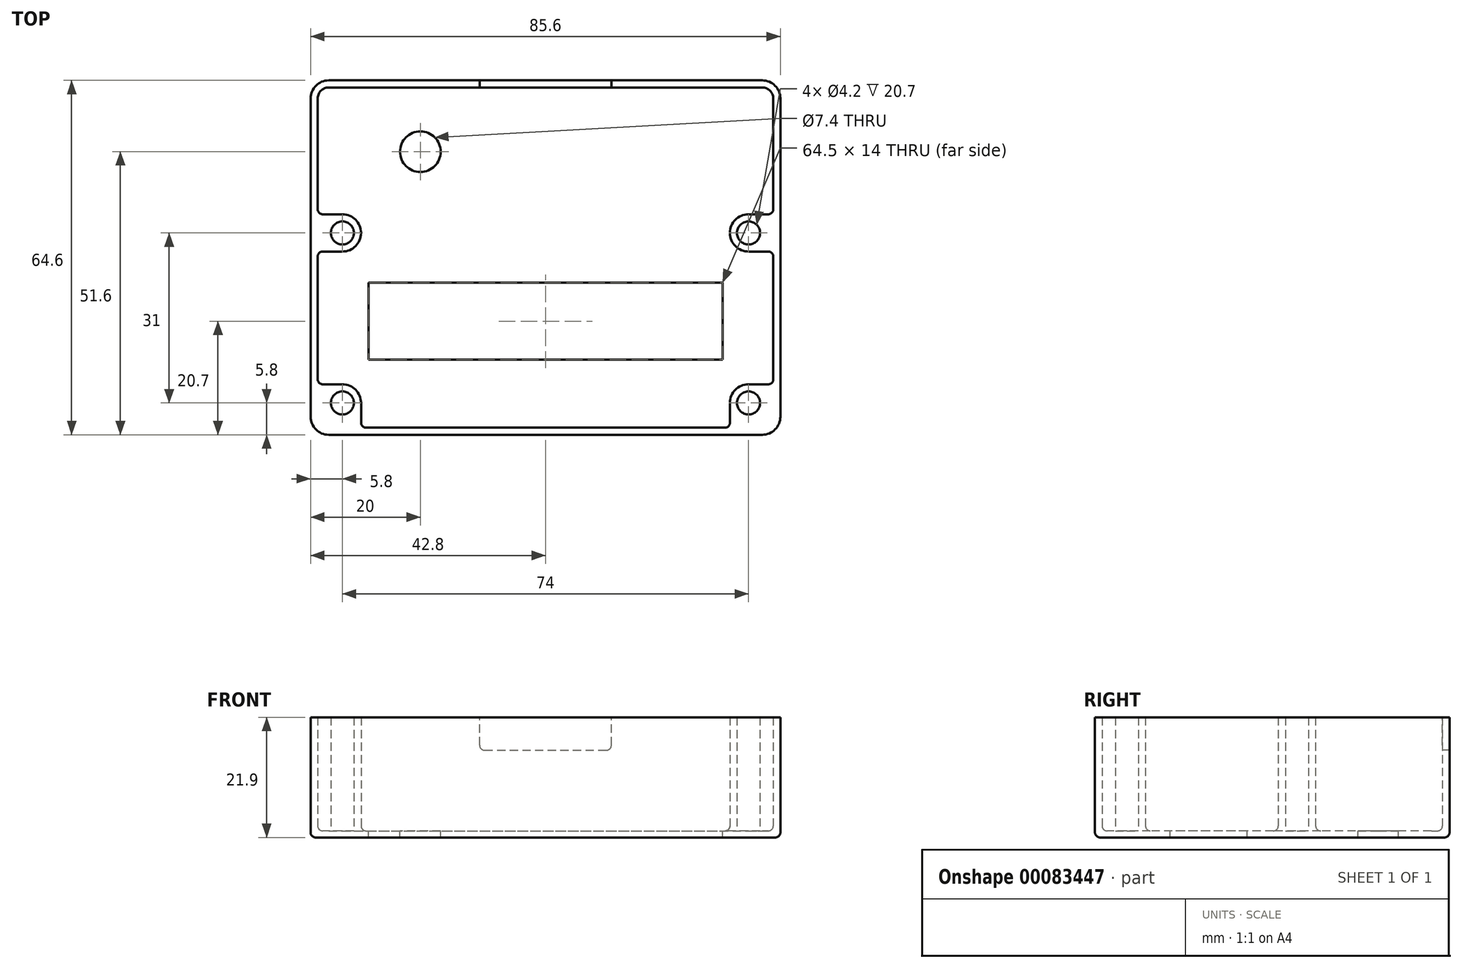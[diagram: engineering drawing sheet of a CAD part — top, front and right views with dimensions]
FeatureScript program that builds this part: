
annotation { "Feature Type Name" : "Feature", "Feature Type Description" : "" }
export const myFeature = defineFeature(function(context is Context, id is Id, definition is map)
    precondition{}
    {
        {
            var Q0;
            Q0=qCreatedBy(makeId("Top.planeOp"),FACE);
            var sketch = newSketch(context, id + "F0", { "sketchPlane" : qUnion([Q0])});
            skLineSegment(sketch, "E0.bottom", {"start": v(-37, 15.5) * mm, "end": v(37, 15.5) * mm, "construction": true});
            skLineSegment(sketch, "E0.top", {"start": v(-37, -15.5) * mm, "end": v(37, -15.5) * mm, "construction": true});
            skLineSegment(sketch, "E0.left", {"start": v(-37, 15.5) * mm, "end": v(-37, -15.5) * mm, "construction": true});
            skLineSegment(sketch, "E0.right", {"start": v(37, 15.5) * mm, "end": v(37, -15.5) * mm, "construction": true});
            skCircle(sketch, "E1", {"center": v(-37, 15.5) * mm, "radius": 2.1 * mm});
            skCircle(sketch, "E2", {"center": v(37, 15.5) * mm, "radius": 2.1 * mm});
            skCircle(sketch, "E3", {"center": v(37, -15.5) * mm, "radius": 2.1 * mm});
            skCircle(sketch, "E4", {"center": v(-37, -15.5) * mm, "radius": 2.1 * mm});
            skLineSegment(sketch, "E5.bottom", {"start": v(-39.5, 42) * mm, "end": v(39.5, 42) * mm});
            skLineSegment(sketch, "E5.top", {"start": v(-39.5, -20) * mm, "end": v(39.5, -20) * mm});
            skLineSegment(sketch, "E5.left", {"start": v(-41.5, 40) * mm, "end": v(-41.5, -18) * mm});
            skLineSegment(sketch, "E5.right", {"start": v(41.5, 40) * mm, "end": v(41.5, -18) * mm});
            skPoint(sketch, "E6.visualSharp", {"position": v(-41.5, 42) * mm});
            skArc(sketch, "E6.filletArc", {"start": v(-39.5, 42) * mm, "mid": v(-40.91, 41.41) * mm, "end": v(-41.5, 40) * mm});
            skPoint(sketch, "E7.visualSharp", {"position": v(41.5, 42) * mm});
            skArc(sketch, "E7.filletArc", {"start": v(41.5, 40) * mm, "mid": v(40.91, 41.41) * mm, "end": v(39.5, 42) * mm});
            skPoint(sketch, "E8.visualSharp", {"position": v(41.5, -20) * mm});
            skArc(sketch, "E8.filletArc", {"start": v(39.5, -20) * mm, "mid": v(40.91, -19.41) * mm, "end": v(41.5, -18) * mm});
            skPoint(sketch, "E9.visualSharp", {"position": v(-41.5, -20) * mm});
            skArc(sketch, "E9.filletArc", {"start": v(-41.5, -18) * mm, "mid": v(-40.91, -19.41) * mm, "end": v(-39.5, -20) * mm});
            skArc(sketch, "E10.0", {"start": v(-39.5, 43.3) * mm, "mid": v(-41.83, 42.33) * mm, "end": v(-42.8, 40) * mm});
            skLineSegment(sketch, "E10.1", {"start": v(-42.8, 40) * mm, "end": v(-42.8, -18) * mm});
            skLineSegment(sketch, "E10.2", {"start": v(-39.5, 43.3) * mm, "end": v(39.5, 43.3) * mm});
            skArc(sketch, "E10.3", {"start": v(-42.8, -18) * mm, "mid": v(-41.83, -20.33) * mm, "end": v(-39.5, -21.3) * mm});
            skArc(sketch, "E10.4", {"start": v(42.8, 40) * mm, "mid": v(41.83, 42.33) * mm, "end": v(39.5, 43.3) * mm});
            skLineSegment(sketch, "E10.5", {"start": v(42.8, 40) * mm, "end": v(42.8, -18) * mm});
            skArc(sketch, "E10.6", {"start": v(39.5, -21.3) * mm, "mid": v(41.83, -20.33) * mm, "end": v(42.8, -18) * mm});
            skLineSegment(sketch, "E10.7", {"start": v(-39.5, -21.3) * mm, "end": v(39.5, -21.3) * mm});
            skCircle(sketch, "E11.0", {"center": v(-37, 15.5) * mm, "radius": 3.4 * mm});
            skCircle(sketch, "E12.0", {"center": v(37, 15.5) * mm, "radius": 3.4 * mm});
            skCircle(sketch, "E13.0", {"center": v(-37, -15.5) * mm, "radius": 3.4 * mm});
            skCircle(sketch, "E14.0", {"center": v(37, -15.5) * mm, "radius": 3.4 * mm});
            skLineSegment(sketch, "E15", {"start": v(-37, 12.1) * mm, "end": v(-41.5, 12.1) * mm});
            skLineSegment(sketch, "E16", {"start": v(-37, -12.1) * mm, "end": v(-41.5, -12.1) * mm});
            skLineSegment(sketch, "E17", {"start": v(-33.6, -15.5) * mm, "end": v(-33.6, -20) * mm});
            skLineSegment(sketch, "E18", {"start": v(-37, 18.9) * mm, "end": v(-41.5, 18.9) * mm});
            skLineSegment(sketch, "E19.MirrorCS", {"start": v(37, 18.9) * mm, "end": v(41.5, 18.9) * mm});
            skLineSegment(sketch, "E20.MirrorCS", {"start": v(37, 12.1) * mm, "end": v(41.5, 12.1) * mm});
            skLineSegment(sketch, "E21.MirrorCS", {"start": v(37, -12.1) * mm, "end": v(41.5, -12.1) * mm});
            skLineSegment(sketch, "E22.MirrorCS", {"start": v(33.6, -15.5) * mm, "end": v(33.6, -20) * mm});
            skSolve(sketch);
        }
        {
            var Q0;
            Q0=makeQuery(id+"F0.imprint","IMPRINT",FACE,{"disambiguationData":[TD([[makeQuery(id+"F0.imprint","IMPRINT",EDGE,{"derivedFrom":sQuery(id+"F0.wireOp",EDGE,"E2")}),-1.0]])]});
            var Q1;
            {var subQ0=sQuery(id+"F0.wireOp",EDGE,"E19.MirrorCS");Q1=makeQuery(id+"F0.imprint","IMPRINT",FACE,{"disambiguationData":[TD([[makeQuery(id+"F0.imprint","IMPRINT",EDGE,{"derivedFrom":subQ0}),-1.0]])]});}
            var Q2;
            Q2=makeQuery(id+"F0.imprint","IMPRINT",FACE,{"disambiguationData":[TD([[makeQuery(id+"F0.imprint","IMPRINT",EDGE,{"derivedFrom":sQuery(id+"F0.wireOp",EDGE,"E5.bottom")}),-1.0]])]});
            var Q3;
            Q3=makeQuery(id+"F0.imprint","IMPRINT",FACE,{"disambiguationData":[TD([[makeQuery(id+"F0.imprint","IMPRINT",EDGE,{"derivedFrom":sQuery(id+"F0.wireOp",EDGE,"E5.bottom")}),1.0]])]});
            var Q4;
            Q4=makeQuery(id+"F0.imprint","IMPRINT",FACE,{"disambiguationData":[TD([[makeQuery(id+"F0.imprint","IMPRINT",EDGE,{"derivedFrom":sQuery(id+"F0.wireOp",EDGE,"E3")}),-1.0]])]});
            var Q5;
            Q5=makeQuery(id+"F0.imprint","IMPRINT",FACE,{"disambiguationData":[TD([[makeQuery(id+"F0.imprint","IMPRINT",EDGE,{"derivedFrom":sQuery(id+"F0.wireOp",EDGE,"E3")}),1.0]])]});
            var Q6;
            Q6=makeQuery(id+"F0.imprint","IMPRINT",FACE,{"disambiguationData":[TD([[makeQuery(id+"F0.imprint","IMPRINT",EDGE,{"derivedFrom":sQuery(id+"F0.wireOp",EDGE,"E2")}),1.0]])]});
            var Q7;
            {var subQ0=sQuery(id+"F0.wireOp",EDGE,"E8.filletArc");Q7=makeQuery(id+"F0.imprint","IMPRINT",FACE,{"disambiguationData":[TD([[makeQuery(id+"F0.imprint","IMPRINT",EDGE,{"derivedFrom":subQ0}),1.0]])]});}
            var Q8;
            Q8=makeQuery(id+"F0.imprint","IMPRINT",FACE,{"disambiguationData":[TD([[makeQuery(id+"F0.imprint","IMPRINT",EDGE,{"derivedFrom":sQuery(id+"F0.wireOp",EDGE,"E1")}),1.0]])]});
            var Q9;
            Q9=makeQuery(id+"F0.imprint","IMPRINT",FACE,{"disambiguationData":[TD([[makeQuery(id+"F0.imprint","IMPRINT",EDGE,{"derivedFrom":sQuery(id+"F0.wireOp",EDGE,"E1")}),-1.0]])]});
            var Q10;
            {var subQ0=sQuery(id+"F0.wireOp",EDGE,"E15");Q10=makeQuery(id+"F0.imprint","IMPRINT",FACE,{"disambiguationData":[TD([[makeQuery(id+"F0.imprint","IMPRINT",EDGE,{"derivedFrom":subQ0}),-1.0]])]});}
            var Q11;
            Q11=makeQuery(id+"F0.imprint","IMPRINT",FACE,{"disambiguationData":[TD([[makeQuery(id+"F0.imprint","IMPRINT",EDGE,{"derivedFrom":sQuery(id+"F0.wireOp",EDGE,"E4")}),1.0]])]});
            var Q12;
            Q12=makeQuery(id+"F0.imprint","IMPRINT",FACE,{"disambiguationData":[TD([[makeQuery(id+"F0.imprint","IMPRINT",EDGE,{"derivedFrom":sQuery(id+"F0.wireOp",EDGE,"E4")}),-1.0]])]});
            var Q13;
            {var subQ3=sQuery(id+"F0.wireOp",EDGE,"E9.filletArc");Q13=makeQuery(id+"F0.imprint","IMPRINT",FACE,{"disambiguationData":[TD([[makeQuery(id+"F0.imprint","IMPRINT",EDGE,{"derivedFrom":subQ3}),1.0]])]});}
            extrude(context, id + "F1", {"entities" : qUnion([Q0, Q1, Q2, Q3, Q4, Q5, Q6, Q7, Q8, Q9, Q10, Q11, Q12, Q13]), "oppositeDirection" : true, "depth" : 1.2 * mm});
        }
        {
            var Q0;
            Q0=makeQuery(id+"F0.imprint","IMPRINT",FACE,{"disambiguationData":[TD([[makeQuery(id+"F0.imprint","IMPRINT",EDGE,{"derivedFrom":sQuery(id+"F0.wireOp",EDGE,"E5.bottom")}),1.0]])]});
            var Q1;
            {var subQ0=sQuery(id+"F0.wireOp",EDGE,"E15");Q1=makeQuery(id+"F0.imprint","IMPRINT",FACE,{"disambiguationData":[TD([[makeQuery(id+"F0.imprint","IMPRINT",EDGE,{"derivedFrom":subQ0}),-1.0]])]});}
            var Q2;
            Q2=makeQuery(id+"F0.imprint","IMPRINT",FACE,{"disambiguationData":[TD([[makeQuery(id+"F0.imprint","IMPRINT",EDGE,{"derivedFrom":sQuery(id+"F0.wireOp",EDGE,"E1")}),-1.0]])]});
            var Q3;
            Q3=makeQuery(id+"F0.imprint","IMPRINT",FACE,{"disambiguationData":[TD([[makeQuery(id+"F0.imprint","IMPRINT",EDGE,{"derivedFrom":sQuery(id+"F0.wireOp",EDGE,"E2")}),-1.0]])]});
            var Q4;
            {var subQ0=sQuery(id+"F0.wireOp",EDGE,"E19.MirrorCS");Q4=makeQuery(id+"F0.imprint","IMPRINT",FACE,{"disambiguationData":[TD([[makeQuery(id+"F0.imprint","IMPRINT",EDGE,{"derivedFrom":subQ0}),-1.0]])]});}
            var Q5;
            {var subQ3=sQuery(id+"F0.wireOp",EDGE,"E9.filletArc");Q5=makeQuery(id+"F0.imprint","IMPRINT",FACE,{"disambiguationData":[TD([[makeQuery(id+"F0.imprint","IMPRINT",EDGE,{"derivedFrom":subQ3}),1.0]])]});}
            var Q6;
            Q6=makeQuery(id+"F0.imprint","IMPRINT",FACE,{"disambiguationData":[TD([[makeQuery(id+"F0.imprint","IMPRINT",EDGE,{"derivedFrom":sQuery(id+"F0.wireOp",EDGE,"E4")}),-1.0]])]});
            var Q7;
            {var subQ0=sQuery(id+"F0.wireOp",EDGE,"E8.filletArc");Q7=makeQuery(id+"F0.imprint","IMPRINT",FACE,{"disambiguationData":[TD([[makeQuery(id+"F0.imprint","IMPRINT",EDGE,{"derivedFrom":subQ0}),1.0]])]});}
            var Q8;
            Q8=makeQuery(id+"F0.imprint","IMPRINT",FACE,{"disambiguationData":[TD([[makeQuery(id+"F0.imprint","IMPRINT",EDGE,{"derivedFrom":sQuery(id+"F0.wireOp",EDGE,"E3")}),-1.0]])]});
            extrude(context, id + "F2", {"entities" : qUnion([Q0, Q1, Q2, Q3, Q4, Q5, Q6, Q7, Q8]), "operationType" : NewBodyOperationType.ADD, "depth" : 20.7 * mm});
        }
        {
            var Q0;
            Q0=makeQuery(id+"F2.opExtrude","CAP_FACE",FACE,{"disambiguationData":[OSD([sQuery(id+"F0.wireOp",EDGE,"E1"),sQuery(id+"F0.wireOp",EDGE,"E2"),sQuery(id+"F0.wireOp",EDGE,"E3"),sQuery(id+"F0.wireOp",EDGE,"E4"),sQuery(id+"F0.wireOp",EDGE,"E5.bottom"),sQuery(id+"F0.wireOp",EDGE,"E5.top"),sQuery(id+"F0.wireOp",EDGE,"E5.left"),sQuery(id+"F0.wireOp",EDGE,"E5.right"),sQuery(id+"F0.wireOp",EDGE,"E6.filletArc"),sQuery(id+"F0.wireOp",EDGE,"E7.filletArc"),sQuery(id+"F0.wireOp",EDGE,"E10.0"),sQuery(id+"F0.wireOp",EDGE,"E10.1"),sQuery(id+"F0.wireOp",EDGE,"E10.2"),sQuery(id+"F0.wireOp",EDGE,"E10.3"),sQuery(id+"F0.wireOp",EDGE,"E10.4"),sQuery(id+"F0.wireOp",EDGE,"E10.5"),sQuery(id+"F0.wireOp",EDGE,"E10.6"),sQuery(id+"F0.wireOp",EDGE,"E10.7"),sQuery(id+"F0.wireOp",EDGE,"E11.0"),sQuery(id+"F0.wireOp",EDGE,"E12.0"),sQuery(id+"F0.wireOp",EDGE,"E13.0"),sQuery(id+"F0.wireOp",EDGE,"E14.0"),sQuery(id+"F0.wireOp",EDGE,"E15"),sQuery(id+"F0.wireOp",EDGE,"E16"),sQuery(id+"F0.wireOp",EDGE,"E17"),sQuery(id+"F0.wireOp",EDGE,"E18"),sQuery(id+"F0.wireOp",EDGE,"E19.MirrorCS"),sQuery(id+"F0.wireOp",EDGE,"E20.MirrorCS"),sQuery(id+"F0.wireOp",EDGE,"E21.MirrorCS"),sQuery(id+"F0.wireOp",EDGE,"E22.MirrorCS")])],"isStart":false});
            var sketch = newSketch(context, id + "F3", { "sketchPlane" : qUnion([Q0])});
            skLineSegment(sketch, "E23", {"start": v(-12, 43.3) * mm, "end": v(-12, 42) * mm});
            skLineSegment(sketch, "E24.MirrorCS", {"start": v(12, 43.3) * mm, "end": v(12, 42) * mm});
            skLineSegment(sketch, "E25.0", {"start": v(-39.5, 43.3) * mm, "end": v(39.5, 43.3) * mm});
            skLineSegment(sketch, "E26.0", {"start": v(-39.5, 42) * mm, "end": v(39.5, 42) * mm});
            skSolve(sketch);
        }
        {
            var Q0;
            {var subQ0=sQuery(id+"F3.wireOp",EDGE,"E23");Q0=makeQuery(id+"F3.imprint","IMPRINT",FACE,{"disambiguationData":[TD([[makeQuery(id+"F3.imprint","IMPRINT",EDGE,{"derivedFrom":subQ0}),1.0]])]});}
            extrude(context, id + "F4", {"entities" : qUnion([Q0]), "operationType" : NewBodyOperationType.REMOVE, "oppositeDirection" : true, "depth" : 6 * mm});
        }
        {
            var Q0;
            Q0=makeQuery(id+"F2.opExtrude","SWEPT_EDGE",EDGE,{"disambiguationData":[OSD([sQuery(id+"F0.wireOp",EDGE,"E5.left"),sQuery(id+"F0.wireOp",EDGE,"E15")])]});
            var Q1;
            Q1=makeQuery(id+"F2.opExtrude","SWEPT_EDGE",EDGE,{"disambiguationData":[OSD([sQuery(id+"F0.wireOp",EDGE,"E5.left"),sQuery(id+"F0.wireOp",EDGE,"E16")])]});
            var Q2;
            Q2=makeQuery(id+"F2.opExtrude","SWEPT_EDGE",EDGE,{"disambiguationData":[OSD([sQuery(id+"F0.wireOp",EDGE,"E5.top"),sQuery(id+"F0.wireOp",EDGE,"E17")])]});
            var Q3;
            Q3=makeQuery(id+"F2.opExtrude","SWEPT_EDGE",EDGE,{"disambiguationData":[OSD([sQuery(id+"F0.wireOp",EDGE,"E5.left"),sQuery(id+"F0.wireOp",EDGE,"E18")])]});
            var Q4;
            Q4=makeQuery(id+"F2.opExtrude","SWEPT_EDGE",EDGE,{"disambiguationData":[OSD([sQuery(id+"F0.wireOp",EDGE,"E5.right"),sQuery(id+"F0.wireOp",EDGE,"E21.MirrorCS")])]});
            var Q5;
            Q5=makeQuery(id+"F2.opExtrude","SWEPT_EDGE",EDGE,{"disambiguationData":[OSD([sQuery(id+"F0.wireOp",EDGE,"E5.top"),sQuery(id+"F0.wireOp",EDGE,"E22.MirrorCS")])]});
            var Q6;
            Q6=makeQuery(id+"F2.opExtrude","SWEPT_EDGE",EDGE,{"disambiguationData":[OSD([sQuery(id+"F0.wireOp",EDGE,"E5.right"),sQuery(id+"F0.wireOp",EDGE,"E19.MirrorCS")])]});
            var Q7;
            Q7=makeQuery(id+"F2.opExtrude","SWEPT_EDGE",EDGE,{"disambiguationData":[OSD([sQuery(id+"F0.wireOp",EDGE,"E5.right"),sQuery(id+"F0.wireOp",EDGE,"E20.MirrorCS")])]});
            var Q8;
            Q8=makeQuery(id+"F2.boolean.opBoolean","SPLIT",FACE,{"disambiguationData":[TD([makeQuery(id+"F2.opExtrude","SWEPT_FACE",FACE,{"disambiguationData":[OSD([sQuery(id+"F0.wireOp",EDGE,"E5.bottom")])]})])],"derivedFrom":makeQuery(id+"F1.opExtrude","CAP_FACE",FACE,{"disambiguationData":[OSD([sQuery(id+"F0.wireOp",EDGE,"E10.0"),sQuery(id+"F0.wireOp",EDGE,"E10.1"),sQuery(id+"F0.wireOp",EDGE,"E10.2"),sQuery(id+"F0.wireOp",EDGE,"E10.3"),sQuery(id+"F0.wireOp",EDGE,"E10.4"),sQuery(id+"F0.wireOp",EDGE,"E10.5"),sQuery(id+"F0.wireOp",EDGE,"E10.6"),sQuery(id+"F0.wireOp",EDGE,"E10.7")])],"isStart":true})});
            var Q9;
            Q9=makeQuery(id+"F1.opExtrude","CAP_FACE",FACE,{"disambiguationData":[OSD([sQuery(id+"F0.wireOp",EDGE,"E10.0"),sQuery(id+"F0.wireOp",EDGE,"E10.1"),sQuery(id+"F0.wireOp",EDGE,"E10.2"),sQuery(id+"F0.wireOp",EDGE,"E10.3"),sQuery(id+"F0.wireOp",EDGE,"E10.4"),sQuery(id+"F0.wireOp",EDGE,"E10.5"),sQuery(id+"F0.wireOp",EDGE,"E10.6"),sQuery(id+"F0.wireOp",EDGE,"E10.7")])],"isStart":false});
            var Q10;
            Q10=makeQuery(id+"F4.boolean.opBoolean","COPY",EDGE,{"derivedFrom":makeQuery(id+"F4.opExtrude","CAP_EDGE",EDGE,{"disambiguationData":[OSD([sQuery(id+"F3.wireOp",EDGE,"E23")])],"isStart":false})});
            var Q11;
            Q11=makeQuery(id+"F4.boolean.opBoolean","COPY",EDGE,{"derivedFrom":makeQuery(id+"F4.opExtrude","CAP_EDGE",EDGE,{"disambiguationData":[OSD([sQuery(id+"F3.wireOp",EDGE,"E24.MirrorCS")])],"isStart":false})});
            fillet(context, id + "F5", {"entities" : qUnion([Q0, Q1, Q2, Q3, Q4, Q5, Q6, Q7, Q8, Q9, Q10, Q11]), "radius" : .9 * mm, "tangentPropagation" : true, "allowEdgeOverflow" : false});
        }
        {
            var Q0;
            Q0=makeQuery(id+"F0.imprint","IMPRINT",FACE,{"disambiguationData":[TD([[makeQuery(id+"F0.imprint","IMPRINT",EDGE,{"derivedFrom":sQuery(id+"F0.wireOp",EDGE,"E5.bottom")}),1.0]])]});
            var Q1;
            {var subQ0=sQuery(id+"F0.wireOp",EDGE,"E15");Q1=makeQuery(id+"F0.imprint","IMPRINT",FACE,{"disambiguationData":[TD([[makeQuery(id+"F0.imprint","IMPRINT",EDGE,{"derivedFrom":subQ0}),-1.0]])]});}
            var Q2;
            Q2=makeQuery(id+"F0.imprint","IMPRINT",FACE,{"disambiguationData":[TD([[makeQuery(id+"F0.imprint","IMPRINT",EDGE,{"derivedFrom":sQuery(id+"F0.wireOp",EDGE,"E1")}),-1.0]])]});
            var Q3;
            Q3=makeQuery(id+"F0.imprint","IMPRINT",FACE,{"disambiguationData":[TD([[makeQuery(id+"F0.imprint","IMPRINT",EDGE,{"derivedFrom":sQuery(id+"F0.wireOp",EDGE,"E5.bottom")}),-1.0]])]});
            var Q4;
            Q4=makeQuery(id+"F0.imprint","IMPRINT",FACE,{"disambiguationData":[TD([[makeQuery(id+"F0.imprint","IMPRINT",EDGE,{"derivedFrom":sQuery(id+"F0.wireOp",EDGE,"E3")}),-1.0]])]});
            var Q5;
            Q5=makeQuery(id+"F0.imprint","IMPRINT",FACE,{"disambiguationData":[TD([[makeQuery(id+"F0.imprint","IMPRINT",EDGE,{"derivedFrom":sQuery(id+"F0.wireOp",EDGE,"E4")}),-1.0]])]});
            var Q6;
            {var subQ3=sQuery(id+"F0.wireOp",EDGE,"E9.filletArc");Q6=makeQuery(id+"F0.imprint","IMPRINT",FACE,{"disambiguationData":[TD([[makeQuery(id+"F0.imprint","IMPRINT",EDGE,{"derivedFrom":subQ3}),1.0]])]});}
            var Q7;
            {var subQ0=sQuery(id+"F0.wireOp",EDGE,"E8.filletArc");Q7=makeQuery(id+"F0.imprint","IMPRINT",FACE,{"disambiguationData":[TD([[makeQuery(id+"F0.imprint","IMPRINT",EDGE,{"derivedFrom":subQ0}),1.0]])]});}
            var Q8;
            Q8=makeQuery(id+"F0.imprint","IMPRINT",FACE,{"disambiguationData":[TD([[makeQuery(id+"F0.imprint","IMPRINT",EDGE,{"derivedFrom":sQuery(id+"F0.wireOp",EDGE,"E2")}),-1.0]])]});
            var Q9;
            {var subQ0=sQuery(id+"F0.wireOp",EDGE,"E19.MirrorCS");Q9=makeQuery(id+"F0.imprint","IMPRINT",FACE,{"disambiguationData":[TD([[makeQuery(id+"F0.imprint","IMPRINT",EDGE,{"derivedFrom":subQ0}),-1.0]])]});}
            extrude(context, id + "F6", {"entities" : qUnion([Q0, Q1, Q2, Q3, Q4, Q5, Q6, Q7, Q8, Q9]), "oppositeDirection" : true, "depth" : 1.2 * mm});
        }
        {
            var Q0;
            Q0=makeQuery(id+"F0.imprint","IMPRINT",FACE,{"disambiguationData":[TD([[makeQuery(id+"F0.imprint","IMPRINT",EDGE,{"derivedFrom":sQuery(id+"F0.wireOp",EDGE,"E5.bottom")}),-1.0]])]});
            var sketch = newSketch(context, id + "F7", { "sketchPlane" : qUnion([Q0])});
            skPoint(sketch, "E27.0", {"position": v(-37, 15.5) * mm});
            skPoint(sketch, "E28.0", {"position": v(-37, -15.5) * mm});
            skPoint(sketch, "E29.0", {"position": v(37, 15.5) * mm});
            skPoint(sketch, "E30.0", {"position": v(37, -15.5) * mm});
            skLineSegment(sketch, "E31.bottom", {"start": v(-32.25, 6.4) * mm, "end": v(32.25, 6.4) * mm});
            skLineSegment(sketch, "E31.top", {"start": v(-32.25, -7.6) * mm, "end": v(32.25, -7.6) * mm});
            skLineSegment(sketch, "E31.left", {"start": v(-32.25, 6.4) * mm, "end": v(-32.25, -7.6) * mm});
            skLineSegment(sketch, "E31.right", {"start": v(32.25, 6.4) * mm, "end": v(32.25, -7.6) * mm});
            skLineSegment(sketch, "E32.0", {"start": v(-39.5, 43.3) * mm, "end": v(39.5, 43.3) * mm});
            skLineSegment(sketch, "E33.0", {"start": v(-42.8, 40) * mm, "end": v(-42.8, -18) * mm});
            skLineSegment(sketch, "E34", {"start": v(-22.8, 43.3) * mm, "end": v(-22.8, 30.3) * mm, "construction": true});
            skLineSegment(sketch, "E35", {"start": v(-22.8, 30.3) * mm, "end": v(-42.8, 30.3) * mm, "construction": true});
            skCircle(sketch, "E36", {"center": v(-22.8, 30.3) * mm, "radius": 3.7 * mm});
            skLineSegment(sketch, "E37.0", {"start": v(-39.5, 42) * mm, "end": v(39.5, 42) * mm});
            skLineSegment(sketch, "E38.0", {"start": v(-37, 18.9) * mm, "end": v(-41.5, 18.9) * mm});
            skSolve(sketch);
        }
        {
            var Q0;
            Q0=makeQuery(id+"F7.imprint","IMPRINT",FACE,{"disambiguationData":[TD([[makeQuery(id+"F7.imprint","IMPRINT",EDGE,{"derivedFrom":sQuery(id+"F7.wireOp",EDGE,"E31.bottom")}),-1.0]])]});
            var Q1;
            Q1=makeQuery(id+"F7.imprint","IMPRINT",FACE,{"disambiguationData":[TD([[makeQuery(id+"F7.imprint","IMPRINT",EDGE,{"derivedFrom":sQuery(id+"F7.wireOp",EDGE,"E36")}),1.0]])]});
            extrude(context, id + "F8", {"entities" : qUnion([Q0, Q1]), "operationType" : NewBodyOperationType.REMOVE, "endBound" : BoundingType.UP_TO_NEXT, "oppositeDirection" : true, "depth" : 25 * mm});
        }
        {
            var Q0;
            Q0=makeQuery(id+"F0.imprint","IMPRINT",FACE,{"disambiguationData":[TD([[makeQuery(id+"F0.imprint","IMPRINT",EDGE,{"derivedFrom":sQuery(id+"F0.wireOp",EDGE,"E5.bottom")}),1.0]])]});
            extrude(context, id + "F9", {"entities" : qUnion([Q0]), "operationType" : NewBodyOperationType.ADD, "depth" : 9.6 * mm});
        }
        {
            var Q0;
            {var subQ0=sQuery(id+"F0.wireOp",EDGE,"E15");Q0=makeQuery(id+"F0.imprint","IMPRINT",FACE,{"disambiguationData":[TD([[makeQuery(id+"F0.imprint","IMPRINT",EDGE,{"derivedFrom":subQ0}),-1.0]])]});}
            var Q1;
            Q1=makeQuery(id+"F0.imprint","IMPRINT",FACE,{"disambiguationData":[TD([[makeQuery(id+"F0.imprint","IMPRINT",EDGE,{"derivedFrom":sQuery(id+"F0.wireOp",EDGE,"E1")}),-1.0]])]});
            var Q2;
            {var subQ3=sQuery(id+"F0.wireOp",EDGE,"E9.filletArc");Q2=makeQuery(id+"F0.imprint","IMPRINT",FACE,{"disambiguationData":[TD([[makeQuery(id+"F0.imprint","IMPRINT",EDGE,{"derivedFrom":subQ3}),1.0]])]});}
            var Q3;
            Q3=makeQuery(id+"F0.imprint","IMPRINT",FACE,{"disambiguationData":[TD([[makeQuery(id+"F0.imprint","IMPRINT",EDGE,{"derivedFrom":sQuery(id+"F0.wireOp",EDGE,"E4")}),-1.0]])]});
            var Q4;
            Q4=makeQuery(id+"F0.imprint","IMPRINT",FACE,{"disambiguationData":[TD([[makeQuery(id+"F0.imprint","IMPRINT",EDGE,{"derivedFrom":sQuery(id+"F0.wireOp",EDGE,"E3")}),-1.0]])]});
            var Q5;
            {var subQ0=sQuery(id+"F0.wireOp",EDGE,"E8.filletArc");Q5=makeQuery(id+"F0.imprint","IMPRINT",FACE,{"disambiguationData":[TD([[makeQuery(id+"F0.imprint","IMPRINT",EDGE,{"derivedFrom":subQ0}),1.0]])]});}
            var Q6;
            {var subQ0=sQuery(id+"F0.wireOp",EDGE,"E19.MirrorCS");Q6=makeQuery(id+"F0.imprint","IMPRINT",FACE,{"disambiguationData":[TD([[makeQuery(id+"F0.imprint","IMPRINT",EDGE,{"derivedFrom":subQ0}),-1.0]])]});}
            var Q7;
            Q7=makeQuery(id+"F0.imprint","IMPRINT",FACE,{"disambiguationData":[TD([[makeQuery(id+"F0.imprint","IMPRINT",EDGE,{"derivedFrom":sQuery(id+"F0.wireOp",EDGE,"E2")}),-1.0]])]});
            extrude(context, id + "F10", {"entities" : qUnion([Q0, Q1, Q2, Q3, Q4, Q5, Q6, Q7]), "operationType" : NewBodyOperationType.ADD, "depth" : 4.2 * mm});
        }
        {
            var Q0;
            Q0=makeQuery(id+"F10.opExtrude","SWEPT_EDGE",EDGE,{"disambiguationData":[OSD([sQuery(id+"F0.wireOp",EDGE,"E5.right"),sQuery(id+"F0.wireOp",EDGE,"E20.MirrorCS")])]});
            var Q1;
            Q1=makeQuery(id+"F10.opExtrude","SWEPT_EDGE",EDGE,{"disambiguationData":[OSD([sQuery(id+"F0.wireOp",EDGE,"E5.right"),sQuery(id+"F0.wireOp",EDGE,"E21.MirrorCS")])]});
            var Q2;
            Q2=makeQuery(id+"F10.opExtrude","SWEPT_EDGE",EDGE,{"disambiguationData":[OSD([sQuery(id+"F0.wireOp",EDGE,"E5.top"),sQuery(id+"F0.wireOp",EDGE,"E22.MirrorCS")])]});
            var Q3;
            Q3=makeQuery(id+"F10.opExtrude","SWEPT_EDGE",EDGE,{"disambiguationData":[OSD([sQuery(id+"F0.wireOp",EDGE,"E5.right"),sQuery(id+"F0.wireOp",EDGE,"E19.MirrorCS")])]});
            var Q4;
            Q4=makeQuery(id+"F10.opExtrude","SWEPT_EDGE",EDGE,{"disambiguationData":[OSD([sQuery(id+"F0.wireOp",EDGE,"E5.left"),sQuery(id+"F0.wireOp",EDGE,"E18")])]});
            var Q5;
            Q5=makeQuery(id+"F10.opExtrude","SWEPT_EDGE",EDGE,{"disambiguationData":[OSD([sQuery(id+"F0.wireOp",EDGE,"E5.left"),sQuery(id+"F0.wireOp",EDGE,"E16")])]});
            var Q6;
            Q6=makeQuery(id+"F10.opExtrude","SWEPT_EDGE",EDGE,{"disambiguationData":[OSD([sQuery(id+"F0.wireOp",EDGE,"E5.top"),sQuery(id+"F0.wireOp",EDGE,"E17")])]});
            var Q7;
            Q7=makeQuery(id+"F10.opExtrude","SWEPT_EDGE",EDGE,{"disambiguationData":[OSD([sQuery(id+"F0.wireOp",EDGE,"E5.left"),sQuery(id+"F0.wireOp",EDGE,"E15")])]});
            var Q8;
            Q8=makeQuery(id+"F9.opExtrude","CAP_EDGE",EDGE,{"disambiguationData":[OSD([sQuery(id+"F0.wireOp",EDGE,"E5.bottom")])],"isStart":true});
            var Q9;
            Q9=makeQuery(id+"F9.opExtrude","CAP_EDGE",EDGE,{"disambiguationData":[OSD([sQuery(id+"F0.wireOp",EDGE,"E6.filletArc")])],"isStart":true});
            var Q10;
            Q10=makeQuery(id+"F6.opExtrude","CAP_EDGE",EDGE,{"disambiguationData":[OSD([sQuery(id+"F0.wireOp",EDGE,"E10.5")])],"isStart":false});
            fillet(context, id + "F11", {"entities" : qUnion([Q0, Q1, Q2, Q3, Q4, Q5, Q6, Q7, Q8, Q9, Q10]), "radius" : .9 * mm, "tangentPropagation" : true, "allowEdgeOverflow" : false});
        }
    });
